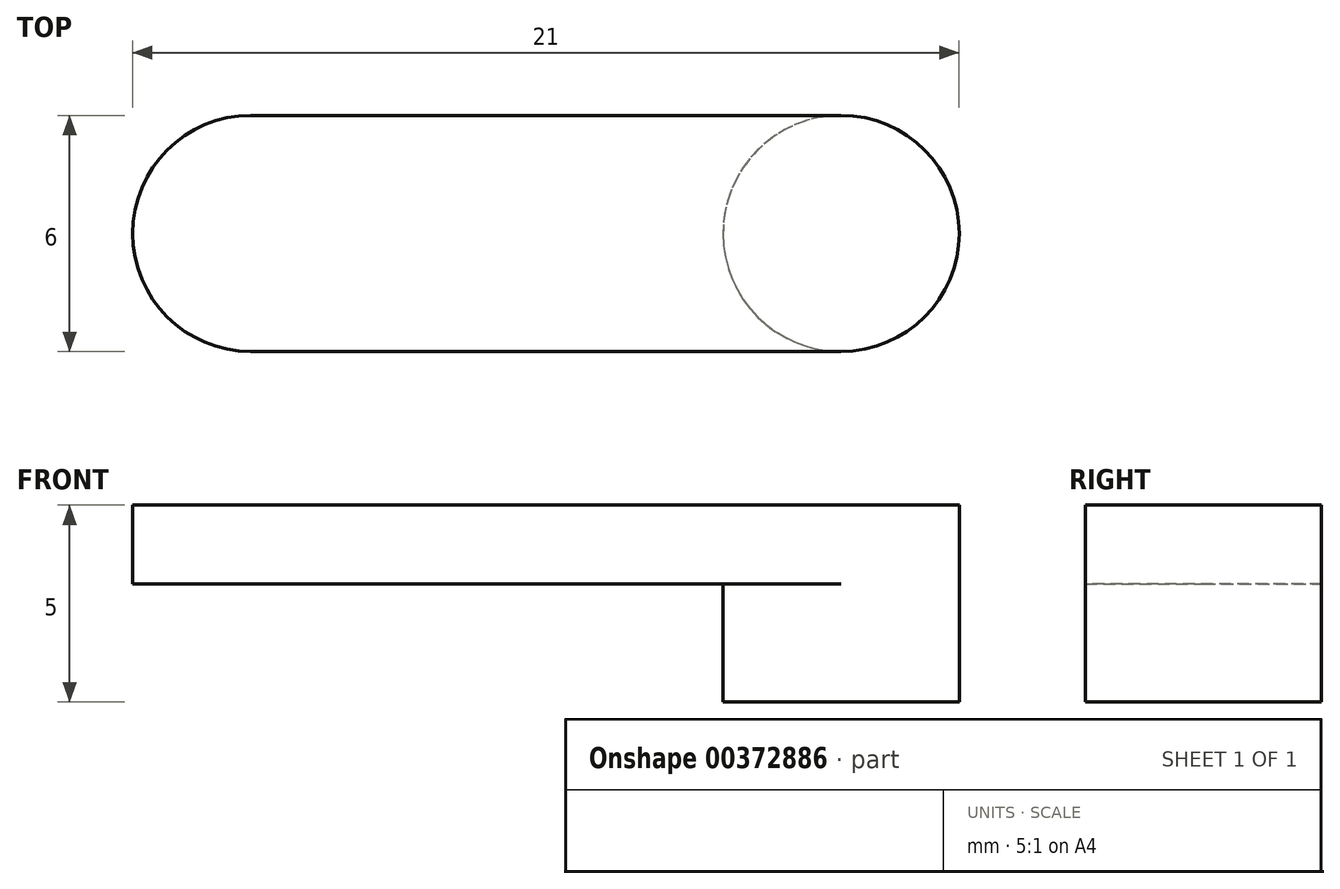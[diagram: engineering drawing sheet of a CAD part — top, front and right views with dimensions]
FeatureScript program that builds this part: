
annotation { "Feature Type Name" : "Feature", "Feature Type Description" : "" }
export const myFeature = defineFeature(function(context is Context, id is Id, definition is map)
    precondition{}
    {
        {
            var Q0;
            Q0=qCreatedBy(makeId("Top.planeOp"),FACE);
            var sketch = newSketch(context, id + "F0", { "sketchPlane" : qUnion([Q0])});
            skLineSegment(sketch, "E0.bottom", {"start": v(-8.75, 1.34) * mm, "end": v(6.25, 1.34) * mm});
            skLineSegment(sketch, "E0.top", {"start": v(-8.75, -4.66) * mm, "end": v(6.25, -4.66) * mm});
            skArc(sketch, "E1", {"start": v(6.25, -4.66) * mm, "mid": v(9.25, -1.66) * mm, "end": v(6.25, 1.34) * mm});
            skArc(sketch, "E2", {"start": v(-8.75, 1.34) * mm, "mid": v(-11.75, -1.66) * mm, "end": v(-8.75, -4.66) * mm});
            skSolve(sketch);
        }
        {
            var Q0;
            Q0 = qSketchRegion(id + "F0", true);
            extrude(context, id + "F1", {"entities" : qUnion([Q0]), "depth" : 2 * mm});
        }
        {
            var Q0;
            Q0=makeQuery(id+"F1.opExtrude","CAP_FACE",FACE,{"disambiguationData":[OSD([sQuery(id+"F0.wireOp",EDGE,"E0.bottom"),sQuery(id+"F0.wireOp",EDGE,"E0.top"),sQuery(id+"F0.wireOp",EDGE,"E1"),sQuery(id+"F0.wireOp",EDGE,"E2")])],"isStart":true});
            cPlane(context, id + "F2", {"entities" : qUnion([Q0]), "cplaneType" : CPlaneType.OFFSET, "offset" : 0 * mm, "width" : 150 * mm, "height" : 150 * mm});
        }
        {
            var Q0;
            Q0=qCreatedBy(id+"F2.planeOp",FACE);
            var sketch = newSketch(context, id + "F3", { "sketchPlane" : qUnion([Q0])});
            skCircle(sketch, "E3", {"center": v(6.25, 1.66) * mm, "radius": 3 * mm});
            skSolve(sketch);
        }
        {
            var Q0;
            Q0 = qSketchRegion(id + "F3", true);
            extrude(context, id + "F4", {"entities" : qUnion([Q0]), "operationType" : NewBodyOperationType.ADD, "depth" : 3 * mm});
        }
    });
